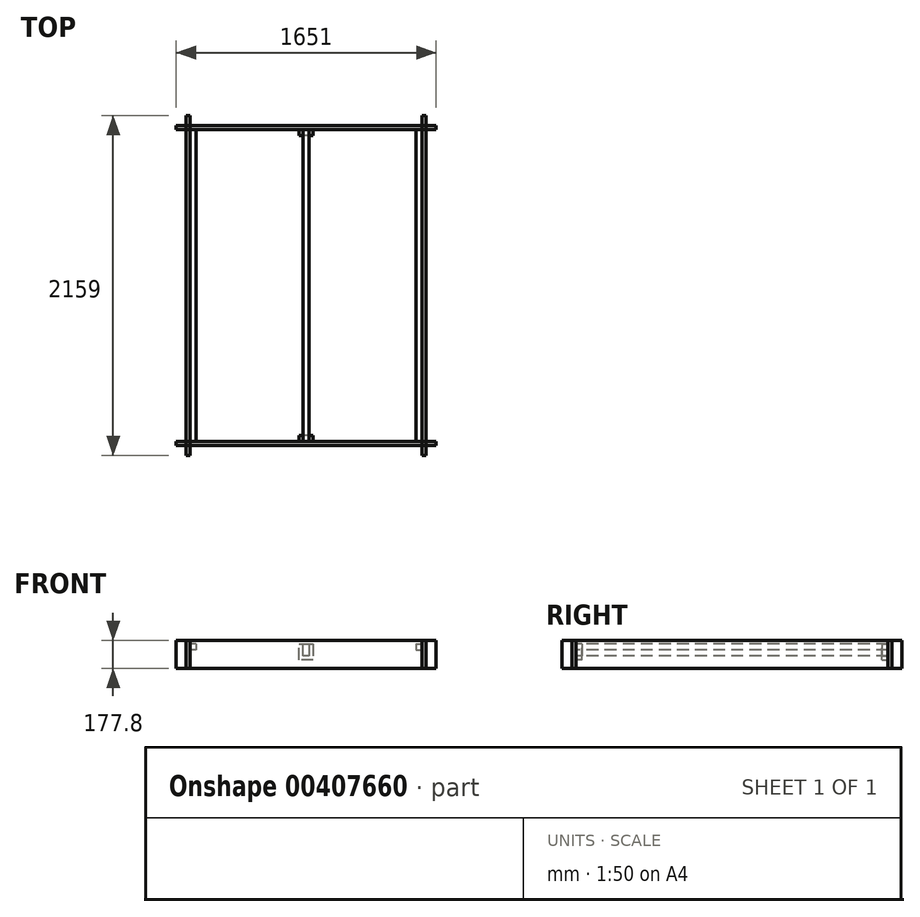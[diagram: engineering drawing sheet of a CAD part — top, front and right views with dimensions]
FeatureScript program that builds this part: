
annotation { "Feature Type Name" : "Feature", "Feature Type Description" : "" }
export const myFeature = defineFeature(function(context is Context, id is Id, definition is map)
    precondition{}
    {
        {
            var Q0;
            Q0=qCreatedBy(makeId("Top.planeOp"),FACE);
            var sketch = newSketch(context, id + "F0", { "sketchPlane" : qUnion([Q0])});
            skLineSegment(sketch, "E0.bottom", {"start": v(-762, 1016) * mm, "end": v(762, 1016) * mm, "construction": true});
            skLineSegment(sketch, "E0.top", {"start": v(-762, -1016) * mm, "end": v(762, -1016) * mm, "construction": true});
            skLineSegment(sketch, "E0.left", {"start": v(-762, 1016) * mm, "end": v(-762, -1016) * mm, "construction": true});
            skLineSegment(sketch, "E0.right", {"start": v(762, 1016) * mm, "end": v(762, -1016) * mm, "construction": true});
            skPoint(sketch, "E0.middle", {"position": v(0, 0) * mm});
            skSolve(sketch);
        }
        {
            var Q0;
            Q0=qCreatedBy(makeId("Top.planeOp"),FACE);
            var sketch = newSketch(context, id + "F1", { "sketchPlane" : qUnion([Q0])});
            skLineSegment(sketch, "E1.bottom", {"start": v(-889, 1143) * mm, "end": v(889, 1143) * mm, "construction": true});
            skLineSegment(sketch, "E1.top", {"start": v(-889, -1143) * mm, "end": v(889, -1143) * mm, "construction": true});
            skLineSegment(sketch, "E1.left", {"start": v(-889, 1143) * mm, "end": v(-889, -1143) * mm, "construction": true});
            skLineSegment(sketch, "E1.right", {"start": v(889, 1143) * mm, "end": v(889, -1143) * mm, "construction": true});
            skPoint(sketch, "E1.middle", {"position": v(0, 0) * mm});
            skSolve(sketch);
        }
        {
            var Q0;
            Q0=qCreatedBy(makeId("Top.planeOp"),FACE);
            var sketch = newSketch(context, id + "F2", { "sketchPlane" : qUnion([Q0])});
            skLineSegment(sketch, "E2.bottom", {"start": v(-825.5, 990.6) * mm, "end": v(825.5, 990.6) * mm});
            skLineSegment(sketch, "E2.top", {"start": v(-825.5, 1016) * mm, "end": v(825.5, 1016) * mm});
            skLineSegment(sketch, "E2.left", {"start": v(-825.5, 990.6) * mm, "end": v(-825.5, 1016) * mm});
            skLineSegment(sketch, "E2.right", {"start": v(825.5, 990.6) * mm, "end": v(825.5, 1016) * mm});
            skPoint(sketch, "E2.middle", {"position": v(0, 1003.3) * mm});
            skSolve(sketch);
        }
        {
            var Q0;
            Q0 = qSketchRegion(id + "F2", true);
            extrude(context, id + "F3", {"entities" : qUnion([Q0]), "depth" : 177.8 * mm});
        }
        {
            var Q0;
            Q0=qCreatedBy(makeId("Top.planeOp"),FACE);
            var sketch = newSketch(context, id + "F4", { "sketchPlane" : qUnion([Q0])});
            skLineSegment(sketch, "E3.bottom", {"start": v(736.6, 1079.5) * mm, "end": v(762, 1079.5) * mm});
            skLineSegment(sketch, "E3.top", {"start": v(736.6, -1079.5) * mm, "end": v(762, -1079.5) * mm});
            skLineSegment(sketch, "E3.left", {"start": v(736.6, 1079.5) * mm, "end": v(736.6, -1079.5) * mm});
            skLineSegment(sketch, "E3.right", {"start": v(762, 1079.5) * mm, "end": v(762, -1079.5) * mm});
            skPoint(sketch, "E3.middle", {"position": v(749.3, 0) * mm});
            skSolve(sketch);
        }
        {
            var Q0;
            Q0 = qSketchRegion(id + "F4", true);
            extrude(context, id + "F5", {"entities" : qUnion([Q0]), "depth" : 177.8 * mm});
        }
        {
            var Q0;
            Q0=qCreatedBy(makeId("Top.planeOp"),FACE);
            cPlane(context, id + "F6", {"entities" : qUnion([Q0]), "cplaneType" : CPlaneType.OFFSET, "offset" : 117.47 * mm, "width" : 152.4 * mm, "height" : 152.4 * mm});
        }
        {
            var Q0;
            Q0=qCreatedBy(id+"F6.planeOp",FACE);
            var sketch = newSketch(context, id + "F7", { "sketchPlane" : qUnion([Q0])});
            skLineSegment(sketch, "E4.0", {"start": v(736.6, 990.6) * mm, "end": v(736.6, -990.6) * mm});
            skLineSegment(sketch, "E5.0", {"start": v(-825.5, 990.6) * mm, "end": v(825.5, 990.6) * mm, "construction": true});
            skPoint(sketch, "E6", {"position": v(736.6, 990.6) * mm});
            skLineSegment(sketch, "E7.0", {"start": v(698.5, 990.6) * mm, "end": v(698.5, -990.6) * mm});
            skLineSegment(sketch, "E8", {"start": v(698.5, 990.6) * mm, "end": v(736.6, 990.6) * mm});
            skLineSegment(sketch, "E9", {"start": v(698.5, -990.6) * mm, "end": v(736.6, -990.6) * mm});
            skSolve(sketch);
        }
        {
            var Q0;
            Q0 = qSketchRegion(id + "F7", true);
            extrude(context, id + "F8", {"entities" : qUnion([Q0]), "depth" : 38.1 * mm});
        }
        {
            var Q0;
            Q0=makeQuery(id+"F3.opExtrude","SWEPT_BODY",BODY,{"disambiguationData":[OSD([sQuery(id+"F2.wireOp",EDGE,"E2.bottom"),sQuery(id+"F2.wireOp",EDGE,"E2.top"),sQuery(id+"F2.wireOp",EDGE,"E2.left"),sQuery(id+"F2.wireOp",EDGE,"E2.right")])]});
            var Q1;
            Q1=qCreatedBy(makeId("Front.planeOp"),FACE);
            mirror(context, id + "F9", {"entities" : qUnion([Q0]), "mirrorPlane" : qUnion([Q1])});
        }
        {
            var Q0;
            Q0=makeQuery(id+"F5.opExtrude","SWEPT_BODY",BODY,{"disambiguationData":[OSD([sQuery(id+"F4.wireOp",EDGE,"E3.bottom"),sQuery(id+"F4.wireOp",EDGE,"E3.top"),sQuery(id+"F4.wireOp",EDGE,"E3.left"),sQuery(id+"F4.wireOp",EDGE,"E3.right")])]});
            var Q1;
            Q1=makeQuery(id+"F8.opExtrude","SWEPT_BODY",BODY,{"disambiguationData":[OSD([sQuery(id+"F7.wireOp",EDGE,"E4.0"),sQuery(id+"F7.wireOp",EDGE,"E7.0"),sQuery(id+"F7.wireOp",EDGE,"E8"),sQuery(id+"F7.wireOp",EDGE,"E9")])]});
            var Q2;
            Q2=qCreatedBy(makeId("Right.planeOp"),FACE);
            mirror(context, id + "F10", {"entities" : qUnion([Q0, Q1]), "mirrorPlane" : qUnion([Q2])});
        }
        {
            var Q0;
            Q0=qCreatedBy(id+"F6.planeOp",FACE);
            var sketch = newSketch(context, id + "F11", { "sketchPlane" : qUnion([Q0])});
            skLineSegment(sketch, "E10.bottom", {"start": v(-19.05, 990.6) * mm, "end": v(19.05, 990.6) * mm});
            skLineSegment(sketch, "E10.top", {"start": v(-19.05, -990.6) * mm, "end": v(19.05, -990.6) * mm});
            skLineSegment(sketch, "E10.left", {"start": v(-19.05, 990.6) * mm, "end": v(-19.05, -990.6) * mm});
            skLineSegment(sketch, "E10.right", {"start": v(19.05, 990.6) * mm, "end": v(19.05, -990.6) * mm});
            skPoint(sketch, "E10.middle", {"position": v(0, 0) * mm});
            skSolve(sketch);
        }
        {
            var Q0;
            Q0 = qSketchRegion(id + "F11", true);
            extrude(context, id + "F12", {"entities" : qUnion([Q0]), "endBound" : BoundingType.SYMMETRIC, "depth" : 76.2 * mm});
        }
        {
            var Q0;
            Q0=makeQuery(id+"F3.opExtrude","SWEPT_FACE",FACE,{"disambiguationData":[OSD([sQuery(id+"F2.wireOp",EDGE,"E2.bottom")])]});
            var sketch = newSketch(context, id + "F13", { "sketchPlane" : qUnion([Q0])});
            skLineSegment(sketch, "E11.0.0", {"start": v(19.05, 79.38) * mm, "end": v(-19.05, 79.38) * mm});
            skLineSegment(sketch, "E11.0.1", {"start": v(-19.05, 79.38) * mm, "end": v(-19.05, 155.58) * mm});
            skLineSegment(sketch, "E11.0.3", {"start": v(19.05, 155.58) * mm, "end": v(19.05, 79.38) * mm});
            skLineSegment(sketch, "E12", {"start": v(19.05, 155.58) * mm, "end": v(44.45, 155.58) * mm});
            skLineSegment(sketch, "E13", {"start": v(44.45, 155.58) * mm, "end": v(44.45, 53.98) * mm});
            skLineSegment(sketch, "E14", {"start": v(44.45, 53.98) * mm, "end": v(-44.45, 53.98) * mm});
            skLineSegment(sketch, "E15", {"start": v(-44.45, 53.98) * mm, "end": v(-44.45, 155.58) * mm});
            skLineSegment(sketch, "E16", {"start": v(-44.45, 155.58) * mm, "end": v(-19.05, 155.58) * mm});
            skSolve(sketch);
        }
        {
            var Q0;
            Q0 = qSketchRegion(id + "F13", true);
            extrude(context, id + "F14", {"entities" : qUnion([Q0]), "depth" : 38.1 * mm});
        }
        {
            var Q0;
            Q0=makeQuery(id+"F14.opExtrude","SWEPT_BODY",BODY,{"disambiguationData":[OSD([sQuery(id+"F13.wireOp",EDGE,"E11.0.0"),sQuery(id+"F13.wireOp",EDGE,"E11.0.1"),sQuery(id+"F13.wireOp",EDGE,"E11.0.3"),sQuery(id+"F13.wireOp",EDGE,"E12"),sQuery(id+"F13.wireOp",EDGE,"E13"),sQuery(id+"F13.wireOp",EDGE,"E14"),sQuery(id+"F13.wireOp",EDGE,"E15"),sQuery(id+"F13.wireOp",EDGE,"E16")])]});
            var Q1;
            Q1=qCreatedBy(makeId("Front.planeOp"),FACE);
            mirror(context, id + "F15", {"entities" : qUnion([Q0]), "mirrorPlane" : qUnion([Q1])});
        }
    });
